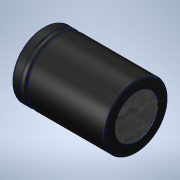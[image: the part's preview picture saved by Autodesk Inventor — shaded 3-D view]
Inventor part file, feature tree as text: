
AUTODESK INVENTOR PART (.ipt)
format: ipt  version: 2020.2 (Build 242310000, 310)  size: 222,208 bytes
history: native  units: mm
features: sketch x4, fillet x3, extrude x3, revolve x1
ambient origin geometry x8: Origin, YZ Plane, XZ Plane, XY Plane, X Axis, Y Axis, Z Axis, Center Point
bodies: Solid1 (feature_tree)
feature tree (11):
  revolve  "Revolution1"  [1 undecoded]
  fillet  "Fillet1"  Radius=3.0mm
  fillet  "Fillet2"  Radius=0.75mm
  fillet  "Fillet3"  Radius=5.0mm
  extrude  "Extrusion1"  Depth=1.0mm
  extrude  "Extrusion2"  Depth=3.0mm
  extrude  "Extrusion3"  Depth=1.0mm
  sketch  "Sketch1"  dims[d0=50.8mm d1=17.575mm d2=3.0mm d3=0.75mm d4=5.0mm]
  sketch  "Sketch2"  dims[d5=90.0deg d6=1.0mm]
  sketch  "Sketch3"  dims[d7=2.0mm d8=3.0mm]
  sketch  "Sketch4"  dims[d9=1.0mm d10=26.5mm d11=1.0mm d12=0.0mm d13=23.5mm d14=0.25mm d15=0.0mm d16=3.0mm d17=3.0mm d18=3.0mm d19=3.0mm d20=1.0mm d21=0.0mm]
note: 1 required parameter value undecoded (feature->parameter linkage not recoverable at this tier; creation-order binding heuristic only, values carry confidence <= 0.55)
